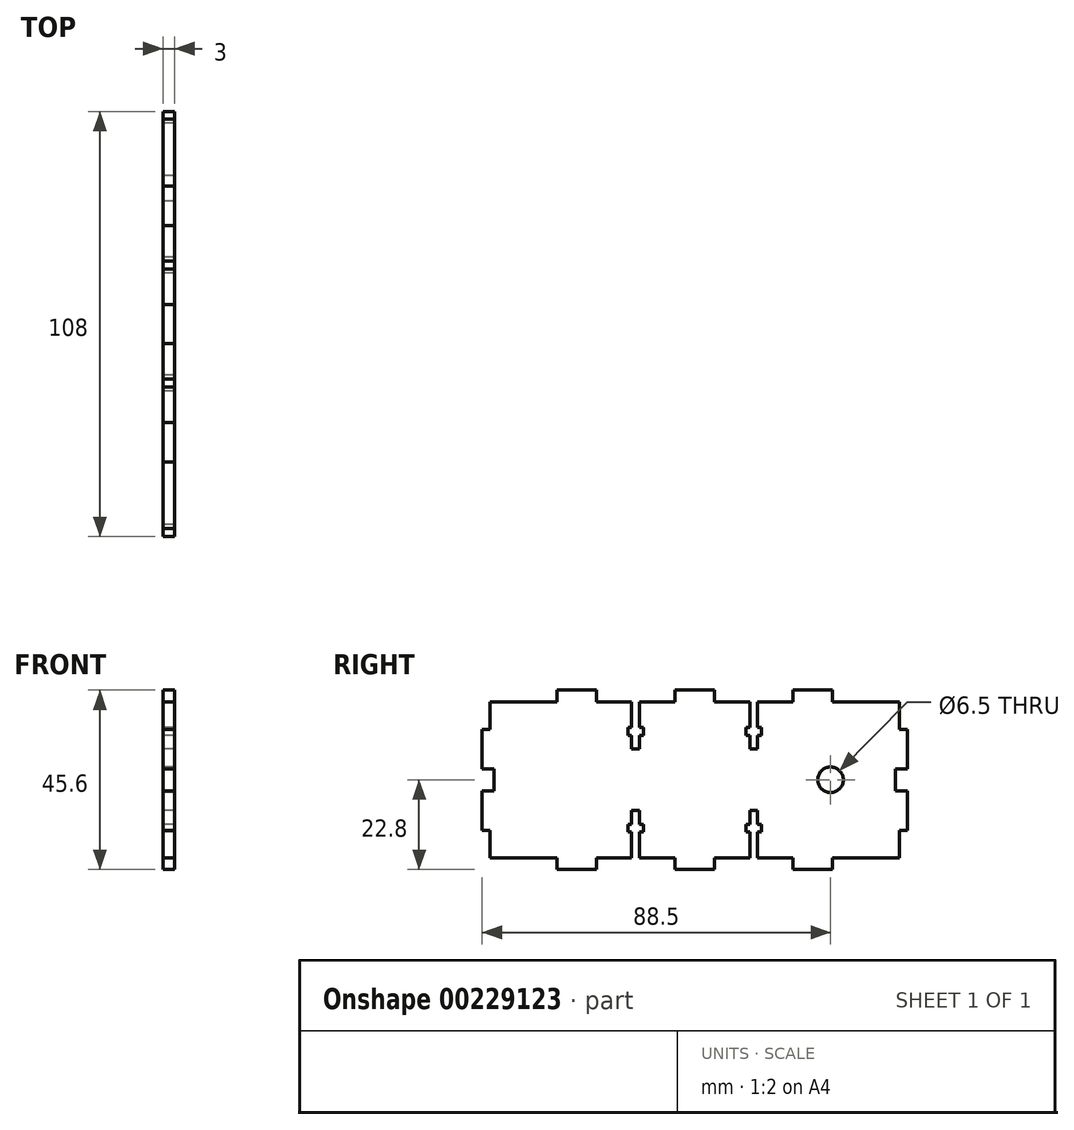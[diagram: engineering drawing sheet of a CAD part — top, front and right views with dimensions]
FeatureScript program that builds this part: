
annotation { "Feature Type Name" : "Feature", "Feature Type Description" : "" }
export const myFeature = defineFeature(function(context is Context, id is Id, definition is map)
    precondition{}
    {
        {
            var Q0;
            Q0=qCreatedBy(makeId("Right.planeOp"),FACE);
            var sketch = newSketch(context, id + "F0", { "sketchPlane" : qUnion([Q0])});
            skLineSegment(sketch, "E0", {"start": v(0, 22.8) * mm, "end": v(0, -22.8) * mm, "construction": true});
            skLineSegment(sketch, "E1.MirrorCS", {"start": v(14, 11.3) * mm, "end": v(13, 11.3) * mm});
            skLineSegment(sketch, "E2.MirrorCS", {"start": v(17, 11.3) * mm, "end": v(16, 11.3) * mm});
            skLineSegment(sketch, "E3.MirrorCS", {"start": v(16, 13.3) * mm, "end": v(17, 13.3) * mm});
            skLineSegment(sketch, "E4.MirrorCS", {"start": v(17, 13.3) * mm, "end": v(17, 11.3) * mm});
            skLineSegment(sketch, "E5.MirrorCS", {"start": v(17, -13.3) * mm, "end": v(17, -11.3) * mm});
            skLineSegment(sketch, "E6.MirrorCS", {"start": v(16, -13.3) * mm, "end": v(17, -13.3) * mm});
            skLineSegment(sketch, "E7.MirrorCS", {"start": v(13, 11.3) * mm, "end": v(13, 13.3) * mm});
            skLineSegment(sketch, "E8.MirrorCS", {"start": v(13, 13.3) * mm, "end": v(14, 13.3) * mm});
            skLineSegment(sketch, "E9.MirrorCS", {"start": v(17, -11.3) * mm, "end": v(16, -11.3) * mm});
            skLineSegment(sketch, "E10.MirrorCS", {"start": v(13, -11.3) * mm, "end": v(13, -13.3) * mm});
            skLineSegment(sketch, "E11.MirrorCS", {"start": v(14, -11.3) * mm, "end": v(13, -11.3) * mm});
            skLineSegment(sketch, "E12.MirrorCS", {"start": v(16, 11.3) * mm, "end": v(16, 7.8) * mm});
            skLineSegment(sketch, "E13.MirrorCS", {"start": v(51, -2.8) * mm, "end": v(51, 0) * mm});
            skLineSegment(sketch, "E14.MirrorCS", {"start": v(14, 7.8) * mm, "end": v(14, 11.3) * mm});
            skLineSegment(sketch, "E15.MirrorCS", {"start": v(51, 2.8) * mm, "end": v(51, 0) * mm});
            skLineSegment(sketch, "E16.MirrorCS", {"start": v(13, -13.3) * mm, "end": v(14, -13.3) * mm});
            skLineSegment(sketch, "E17.MirrorCS", {"start": v(25, -22.8) * mm, "end": v(25, -19.8) * mm});
            skLineSegment(sketch, "E18.MirrorCS", {"start": v(14, -13.3) * mm, "end": v(14, -19.8) * mm});
            skLineSegment(sketch, "E19.MirrorCS", {"start": v(5, -22.8) * mm, "end": v(0, -22.8) * mm});
            skLineSegment(sketch, "E20.MirrorCS", {"start": v(54, -2.8) * mm, "end": v(51, -2.8) * mm});
            skLineSegment(sketch, "E21.MirrorCS", {"start": v(5, 19.8) * mm, "end": v(5, 22.8) * mm});
            skLineSegment(sketch, "E22.MirrorCS", {"start": v(16, -11.3) * mm, "end": v(16, -7.8) * mm});
            skLineSegment(sketch, "E23.MirrorCS", {"start": v(16, -19.8) * mm, "end": v(16, -13.3) * mm});
            skLineSegment(sketch, "E24.MirrorCS", {"start": v(35, -19.8) * mm, "end": v(35, -22.8) * mm});
            skLineSegment(sketch, "E25.MirrorCS", {"start": v(52, 12.8) * mm, "end": v(54, 12.8) * mm});
            skLineSegment(sketch, "E26.MirrorCS", {"start": v(54, 2.8) * mm, "end": v(51, 2.8) * mm});
            skLineSegment(sketch, "E27.MirrorCS", {"start": v(14, -7.8) * mm, "end": v(14, -11.3) * mm});
            skLineSegment(sketch, "E28.MirrorCS", {"start": v(5, 22.8) * mm, "end": v(0, 22.8) * mm});
            skLineSegment(sketch, "E29.MirrorCS", {"start": v(35, 19.8) * mm, "end": v(35, 22.8) * mm});
            skLineSegment(sketch, "E30.MirrorCS", {"start": v(5, -19.8) * mm, "end": v(5, -22.8) * mm});
            skLineSegment(sketch, "E31.MirrorCS", {"start": v(25, 22.8) * mm, "end": v(25, 19.8) * mm});
            skLineSegment(sketch, "E32.MirrorCS", {"start": v(14, -7.8) * mm, "end": v(16, -7.8) * mm});
            skLineSegment(sketch, "E33.MirrorCS", {"start": v(14, 7.8) * mm, "end": v(16, 7.8) * mm});
            skLineSegment(sketch, "E34.MirrorCS", {"start": v(52, -12.8) * mm, "end": v(54, -12.8) * mm});
            skLineSegment(sketch, "E35.MirrorCS", {"start": v(14, 13.3) * mm, "end": v(14, 19.8) * mm});
            skPoint(sketch, "E36.MirrorP", {"position": v(15.5, 11.3) * mm});
            skLineSegment(sketch, "E37.MirrorCS", {"start": v(16, 19.8) * mm, "end": v(16, 13.3) * mm});
            skLineSegment(sketch, "E38.MirrorCS", {"start": v(35, -22.8) * mm, "end": v(25, -22.8) * mm});
            skLineSegment(sketch, "E39.MirrorCS", {"start": v(51, 0) * mm, "end": v(2, 0) * mm, "construction": true});
            skPoint(sketch, "E40.MirrorP", {"position": v(15.5, -11.3) * mm});
            skLineSegment(sketch, "E41.MirrorCS", {"start": v(14, -19.8) * mm, "end": v(5, -19.8) * mm});
            skPoint(sketch, "E42.MirrorP", {"position": v(15.5, 13.3) * mm});
            skLineSegment(sketch, "E43.MirrorCS", {"start": v(25, -19.8) * mm, "end": v(16, -19.8) * mm});
            skLineSegment(sketch, "E44.MirrorCS", {"start": v(52, -19.8) * mm, "end": v(35, -19.8) * mm});
            skPoint(sketch, "E45.MirrorP", {"position": v(15.5, -13.3) * mm});
            skLineSegment(sketch, "E46.MirrorCS", {"start": v(52, 19.8) * mm, "end": v(52, 12.8) * mm});
            skLineSegment(sketch, "E47.MirrorCS", {"start": v(54, 12.8) * mm, "end": v(54, 2.8) * mm});
            skLineSegment(sketch, "E48.MirrorCS", {"start": v(54, -12.8) * mm, "end": v(54, -2.8) * mm});
            skLineSegment(sketch, "E49.MirrorCS", {"start": v(52, 19.8) * mm, "end": v(35, 19.8) * mm});
            skLineSegment(sketch, "E50.MirrorCS", {"start": v(35, 22.8) * mm, "end": v(25, 22.8) * mm});
            skLineSegment(sketch, "E51.MirrorCS", {"start": v(25, 19.8) * mm, "end": v(16, 19.8) * mm});
            skLineSegment(sketch, "E52.MirrorCS", {"start": v(52, -19.8) * mm, "end": v(52, -12.8) * mm});
            skLineSegment(sketch, "E53.MirrorCS", {"start": v(14, 19.8) * mm, "end": v(5, 19.8) * mm});
            skLineSegment(sketch, "E54.MirrorCS", {"start": v(-17, -11.3) * mm, "end": v(-16, -11.3) * mm});
            skLineSegment(sketch, "E55.MirrorCS", {"start": v(-13, 11.3) * mm, "end": v(-13, 13.3) * mm});
            skLineSegment(sketch, "E56.MirrorCS", {"start": v(-14, 11.3) * mm, "end": v(-13, 11.3) * mm});
            skLineSegment(sketch, "E57.MirrorCS", {"start": v(-17, -13.3) * mm, "end": v(-17, -11.3) * mm});
            skLineSegment(sketch, "E58.MirrorCS", {"start": v(-17, 11.3) * mm, "end": v(-16, 11.3) * mm});
            skLineSegment(sketch, "E59.MirrorCS", {"start": v(-16, 13.3) * mm, "end": v(-17, 13.3) * mm});
            skLineSegment(sketch, "E60.MirrorCS", {"start": v(-13, -13.3) * mm, "end": v(-14, -13.3) * mm});
            skLineSegment(sketch, "E61.MirrorCS", {"start": v(-13, 13.3) * mm, "end": v(-14, 13.3) * mm});
            skLineSegment(sketch, "E62.MirrorCS", {"start": v(-17, 13.3) * mm, "end": v(-17, 11.3) * mm});
            skLineSegment(sketch, "E63.MirrorCS", {"start": v(-16, -13.3) * mm, "end": v(-17, -13.3) * mm});
            skLineSegment(sketch, "E64.MirrorCS", {"start": v(-25, 22.8) * mm, "end": v(-25, 19.8) * mm});
            skLineSegment(sketch, "E65.MirrorCS", {"start": v(-54, 2.8) * mm, "end": v(-51, 2.8) * mm});
            skLineSegment(sketch, "E66.MirrorCS", {"start": v(-51, -2.8) * mm, "end": v(-51, 0) * mm});
            skLineSegment(sketch, "E67.MirrorCS", {"start": v(-14, 7.8) * mm, "end": v(-14, 11.3) * mm});
            skLineSegment(sketch, "E68.MirrorCS", {"start": v(-35, 19.8) * mm, "end": v(-35, 22.8) * mm});
            skLineSegment(sketch, "E69.MirrorCS", {"start": v(-54, -2.8) * mm, "end": v(-51, -2.8) * mm});
            skLineSegment(sketch, "E70.MirrorCS", {"start": v(-5, 19.8) * mm, "end": v(-5, 22.8) * mm});
            skLineSegment(sketch, "E71.MirrorCS", {"start": v(-16, 11.3) * mm, "end": v(-16, 7.8) * mm});
            skLineSegment(sketch, "E72.MirrorCS", {"start": v(-14, -11.3) * mm, "end": v(-13, -11.3) * mm});
            skLineSegment(sketch, "E73.MirrorCS", {"start": v(-16, -11.3) * mm, "end": v(-16, -7.8) * mm});
            skLineSegment(sketch, "E74.MirrorCS", {"start": v(-5, -19.8) * mm, "end": v(-5, -22.8) * mm});
            skLineSegment(sketch, "E75.MirrorCS", {"start": v(-14, -7.8) * mm, "end": v(-14, -11.3) * mm});
            skLineSegment(sketch, "E76.MirrorCS", {"start": v(-25, -22.8) * mm, "end": v(-25, -19.8) * mm});
            skLineSegment(sketch, "E77.MirrorCS", {"start": v(-14, -7.8) * mm, "end": v(-16, -7.8) * mm});
            skLineSegment(sketch, "E78.MirrorCS", {"start": v(-14, 7.8) * mm, "end": v(-16, 7.8) * mm});
            skLineSegment(sketch, "E79.MirrorCS", {"start": v(-52, 12.8) * mm, "end": v(-54, 12.8) * mm});
            skLineSegment(sketch, "E80.MirrorCS", {"start": v(-35, -19.8) * mm, "end": v(-35, -22.8) * mm});
            skLineSegment(sketch, "E81.MirrorCS", {"start": v(-13, -11.3) * mm, "end": v(-13, -13.3) * mm});
            skLineSegment(sketch, "E82.MirrorCS", {"start": v(-52, -12.8) * mm, "end": v(-54, -12.8) * mm});
            skLineSegment(sketch, "E83.MirrorCS", {"start": v(-51, 2.8) * mm, "end": v(-51, 0) * mm});
            skLineSegment(sketch, "E84.MirrorCS", {"start": v(-25, 19.8) * mm, "end": v(-16, 19.8) * mm});
            skLineSegment(sketch, "E85.MirrorCS", {"start": v(-16, 19.8) * mm, "end": v(-16, 13.3) * mm});
            skLineSegment(sketch, "E86.MirrorCS", {"start": v(-51, 0) * mm, "end": v(-2, 0) * mm, "construction": true});
            skPoint(sketch, "E87.MirrorP", {"position": v(-15.5, -11.3) * mm});
            skLineSegment(sketch, "E88.MirrorCS", {"start": v(-14, 13.3) * mm, "end": v(-14, 19.8) * mm});
            skLineSegment(sketch, "E89.MirrorCS", {"start": v(-35, 22.8) * mm, "end": v(-25, 22.8) * mm});
            skPoint(sketch, "E90.MirrorP", {"position": v(-15.5, -13.3) * mm});
            skLineSegment(sketch, "E91.MirrorCS", {"start": v(-52, 19.8) * mm, "end": v(-35, 19.8) * mm});
            skLineSegment(sketch, "E92.MirrorCS", {"start": v(-52, -19.8) * mm, "end": v(-52, -12.8) * mm});
            skPoint(sketch, "E93.MirrorP", {"position": v(-15.5, 13.3) * mm});
            skLineSegment(sketch, "E94.MirrorCS", {"start": v(-25, -19.8) * mm, "end": v(-16, -19.8) * mm});
            skLineSegment(sketch, "E95.MirrorCS", {"start": v(-16, -19.8) * mm, "end": v(-16, -13.3) * mm});
            skLineSegment(sketch, "E96.MirrorCS", {"start": v(-35, -22.8) * mm, "end": v(-25, -22.8) * mm});
            skLineSegment(sketch, "E97.MirrorCS", {"start": v(-52, -19.8) * mm, "end": v(-35, -19.8) * mm});
            skLineSegment(sketch, "E98.MirrorCS", {"start": v(-52, 19.8) * mm, "end": v(-52, 12.8) * mm});
            skPoint(sketch, "E99.MirrorP", {"position": v(-15.5, 11.3) * mm});
            skLineSegment(sketch, "E100.MirrorCS", {"start": v(-14, -13.3) * mm, "end": v(-14, -19.8) * mm});
            skLineSegment(sketch, "E101.MirrorCS", {"start": v(-14, -19.8) * mm, "end": v(-5, -19.8) * mm});
            skLineSegment(sketch, "E102.MirrorCS", {"start": v(-14, 19.8) * mm, "end": v(-5, 19.8) * mm});
            skLineSegment(sketch, "E103.MirrorCS", {"start": v(-54, 12.8) * mm, "end": v(-54, 2.8) * mm});
            skLineSegment(sketch, "E104.MirrorCS", {"start": v(-54, -12.8) * mm, "end": v(-54, -2.8) * mm});
            skLineSegment(sketch, "E105", {"start": v(-5, 22.8) * mm, "end": v(0, 22.8) * mm});
            skLineSegment(sketch, "E106", {"start": v(-5, -22.8) * mm, "end": v(0, -22.8) * mm});
            skLineSegment(sketch, "E107", {"start": v(51, 2.8) * mm, "end": v(34.5, 2.8) * mm});
            skCircle(sketch, "E108", {"center": v(34.5, 0) * mm, "radius": 3.25 * mm});
            skSolve(sketch);
        }
        {
            var Q0;
            Q0=makeQuery(id+"F0.imprint","IMPRINT",FACE,{"disambiguationData":[TD([[makeQuery(id+"F0.imprint","IMPRINT",EDGE,{"derivedFrom":sQuery(id+"F0.wireOp",EDGE,"E1.MirrorCS")}),1.0]])]});
            extrude(context, id + "F1", {"entities" : qUnion([Q0]), "depth" : 3 * mm});
        }
    });
